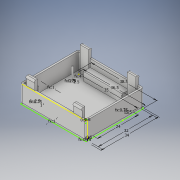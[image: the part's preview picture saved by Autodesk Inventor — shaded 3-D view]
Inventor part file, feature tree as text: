
AUTODESK INVENTOR PART (.ipt)
format: ipt  version: 2019 (Build 230136000, 136)  size: 268,800 bytes
history: native  units: in
note: dims shown in document units (in); Inventor stores cm internally (conversion verified against a paired STEP export)
features: sketch x6, extrude x5, fillet x3, other x1
ambient origin geometry x8: Origin, YZ Plane, XZ Plane, XY Plane, X Axis, Y Axis, Z Axis, Center Point
bodies: Solid1 (feature_tree)
feature tree (15):
  sketch  "Sketch1"  dims[d10=0.0295in d16=0.0295in]
  extrude  "Extrusion1"  Depth=0.0295in
  extrude  "Extrusion2"  Depth=0.315in TaperAngle=0.0deg
  extrude  "Extrusion6"  Depth=0.0394in
  fillet  "Fillet1"  Radius=0.0394in
  sketch  "Sketch14"  dims[d19=0.4134in d20=0.0in d21=0.315in d22=0.0in]
  sketch  "Sketch17"  dims[d35=0.0394in d36=0.0in d46=0.0394in d103=0.0394in d104=0.0197in d105=0.0197in]
  fillet  "Fillet3"  Radius=0.0197in
  other  "Snap Fit6"
  fillet  "Fillet4"  Radius=0.0197in
  sketch  "Sketch24"  dims[d108=0.0394in d120=0.0984in]
  sketch  "Sketch25"  dims[d121=0.0984in d125=0.0541in d126=0.0591in d130=0.0315in d131=0.0197in d132=0.3436in d133=0.3436in d136=0.0197in d137=0.0197in d138=0.0197in d139=0.0197in d140=0.0197in d141=0.0394in d143=0.0837in d145=0.0837in d150=0.1575in d151=0.0295in d153=0.1181in d154=0.0394in d155=1.378in d156=0.9449in d157=0.0984in d158=0.1181in d159=0.0984in d160=0.0837in d162=0.1969in d164=0.0984in d165=0.0in d166=0.1969in d167=0.1575in d168=0.0in d175=0.0492in]
  extrude  "Extrusion9"  Depth=0.0197in
  extrude  "Extrusion10"  Depth=0.0984in
  sketch  "Sketch20"  dims[d106=0.0197in d107=0.0197in]
